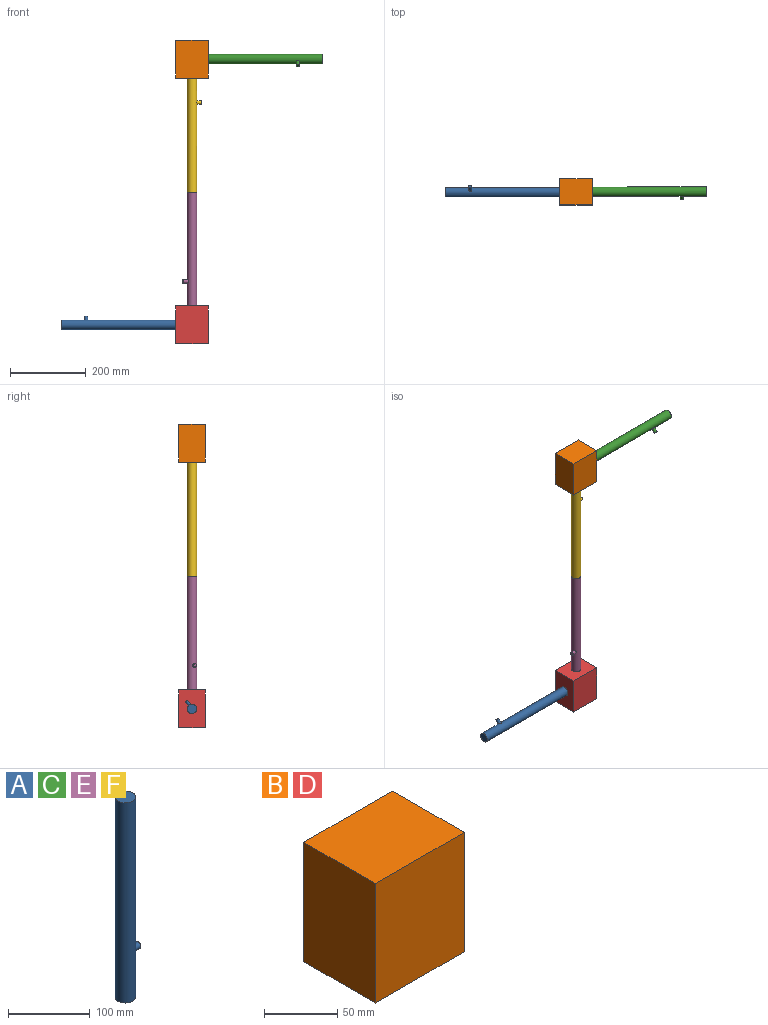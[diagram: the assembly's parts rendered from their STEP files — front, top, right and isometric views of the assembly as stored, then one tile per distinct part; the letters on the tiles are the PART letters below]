
ASSEMBLY  parts=6 mates=5
PART A: 5 faces, bbox 37.5x25x300 mm
  f0: cylinder r=12.5mm len=300mm, axis (0,0,-1), area 23500.9mm2, adj f1,f2,f3
  f1: plane 25x25mm, normal (0,0,1), area 490.9mm2, adj f0
  f2: plane 25x25mm, normal (0,0,-1), area 490.9mm2, adj f0
  f3: cylinder r=4.32mm len=14.45mm, axis (-1,0,0), area 356.8mm2, adj f0,f4
  f4: plane 8.65x8.65mm, normal (1,0,0), area 58.7mm2, adj f3
PART B: 6 faces, bbox 85.9x69.4x100 mm
  f0: plane 100x85.91mm, normal (0,-1,0), area 8591.2mm2, adj f1,f3,f4,f5
  f1: plane 100x69.36mm, normal (1,0,0), area 6935.9mm2, adj f0,f2,f4,f5
  f2: plane 100x85.91mm, normal (0,1,0), area 8591.2mm2, adj f1,f3,f4,f5
  f3: plane 100x69.36mm, normal (-1,0,0), area 6935.9mm2, adj f0,f2,f4,f5
  f4: plane 85.91x69.36mm, normal (0,0,1), area 5958.7mm2, adj f0,f1,f2,f3
  f5: plane 85.91x69.36mm, normal (0,0,-1), area 5958.7mm2, adj f0,f1,f2,f3
PART C: same geometry as A
PART D: same geometry as B
PART E: same geometry as A
PART F: same geometry as A
PLACE A rot(axis=(0.68,0.26,0.68),151.2deg) t=(-599.71,-10.77,205.63)mm
PLACE B rot(axis=(0,-1,0),180deg) t=(-256.76,-10.77,955.63)mm
PLACE C rot(axis=(0.68,-0.26,-0.68),151.2deg) t=(86.2,-10.55,905.63)mm
PLACE D t=(-256.76,-10.77,155.63)mm
PLACE E rot(axis=(0,0,-1),164.6deg) t=(-256.76,-10.77,255.63)mm
PLACE F rot(axis=(-0.99,-0.13,0),180deg) t=(-256.76,-10.77,855.63)mm
MATE revolute E.f0 <-> D.f4  axis (0,0,-1) through (-256.76,-10.77,255.63)mm
MATE fastened F.f0 <-> E.f0  axis (0,0,-1) through (-256.76,-10.77,555.63)mm
MATE revolute C.f0 <-> B.f3  axis (-1,0,0) through (-213.8,-10.74,905.63)mm
MATE revolute F.f0 <-> B.f4  axis (0,0,1) through (-256.76,-10.77,855.63)mm
MATE revolute A.f0 <-> D.f3  axis (1,0,0) through (-299.71,-10.77,205.63)mm
